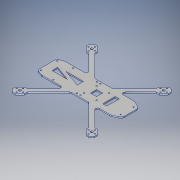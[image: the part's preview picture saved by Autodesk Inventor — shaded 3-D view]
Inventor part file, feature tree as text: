
AUTODESK INVENTOR PART (.ipt)
format: ipt  version: 2019 (Build 230136000, 136)  size: 371,200 bytes
history: native  units: mm
features: extrude x2, sketch x2, projected_geometry x1
ambient origin geometry x8: Origin, YZ Plane, XZ Plane, XY Plane, X Axis, Y Axis, Z Axis, Center Point
bodies: Body1 (feature_tree)
feature tree (5):
  extrude  "Wyciągnięcie proste5"  Depth=250.0mm
  extrude  "Wyciągnięcie proste6"  TaperAngle=135.0deg  [1 undecoded]
  sketch  "Szkic1"
  sketch  "Szkic2"
  projected_geometry  "Pętla rzutowana1"
note: 1 required parameter value undecoded (feature->parameter linkage not recoverable at this tier; creation-order binding heuristic only, values carry confidence <= 0.55)
